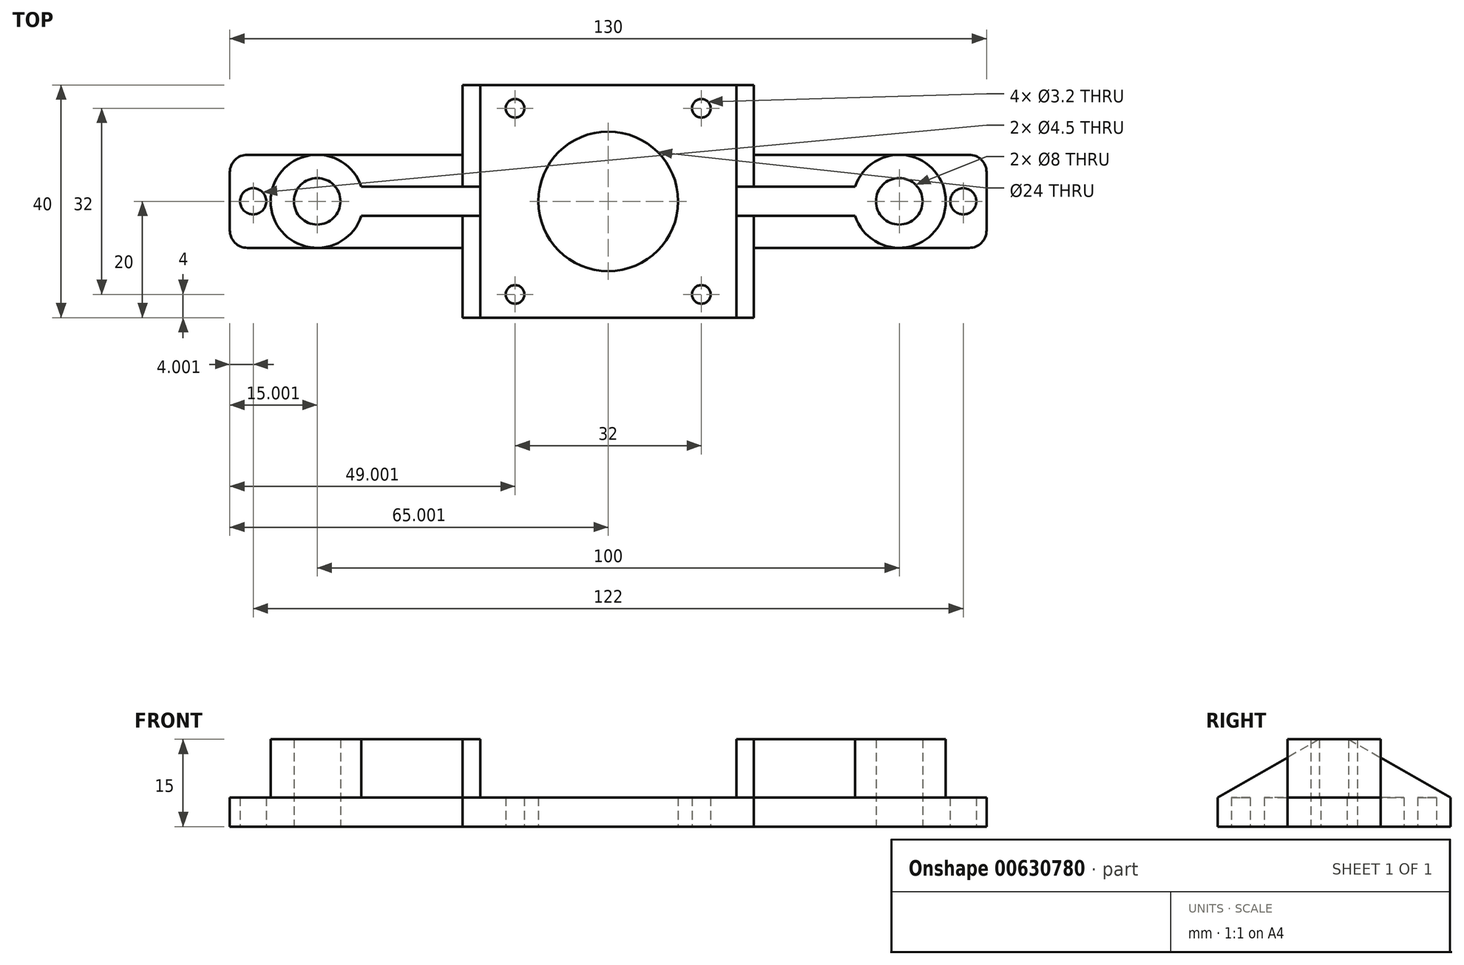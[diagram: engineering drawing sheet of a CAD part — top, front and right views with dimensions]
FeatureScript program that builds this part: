
annotation { "Feature Type Name" : "Feature", "Feature Type Description" : "" }
export const myFeature = defineFeature(function(context is Context, id is Id, definition is map)
    precondition{}
    {
        {
            var Q0;
            Q0=qCreatedBy(makeId("Top.planeOp"),FACE);
            var sketch = newSketch(context, id + "F0", { "sketchPlane" : qUnion([Q0])});
            skCircle(sketch, "E0", {"center": v(-20.16, 0) * mm, "radius": 4 * mm});
            skCircle(sketch, "E1", {"center": v(-20.16, 0) * mm, "radius": 8 * mm});
            skCircle(sketch, "E2", {"center": v(79.84, 0) * mm, "radius": 4 * mm});
            skCircle(sketch, "E3", {"center": v(79.84, 0) * mm, "radius": 8 * mm});
            skLineSegment(sketch, "E4.bottom", {"start": v(-32.16, 8) * mm, "end": v(4.84, 8) * mm});
            skLineSegment(sketch, "E4.top", {"start": v(-32.16, -8) * mm, "end": v(4.84, -8) * mm});
            skLineSegment(sketch, "E4.left", {"start": v(-35.16, 5) * mm, "end": v(-35.16, -5) * mm});
            skLineSegment(sketch, "E4.right", {"start": v(94.84, 5) * mm, "end": v(94.84, -5) * mm});
            skCircle(sketch, "E5", {"center": v(-31.16, 0) * mm, "radius": 2.25 * mm});
            skCircle(sketch, "E6", {"center": v(90.84, 0) * mm, "radius": 2.25 * mm});
            skPoint(sketch, "E7.visualSharp", {"position": v(94.84, 8) * mm});
            skArc(sketch, "E7.filletArc", {"start": v(94.84, 5) * mm, "mid": v(93.96, 7.12) * mm, "end": v(91.84, 8) * mm});
            skPoint(sketch, "E8.visualSharp", {"position": v(94.84, -8) * mm});
            skArc(sketch, "E8.filletArc", {"start": v(91.84, -8) * mm, "mid": v(93.96, -7.12) * mm, "end": v(94.84, -5) * mm});
            skPoint(sketch, "E9.visualSharp", {"position": v(-35.16, -8) * mm});
            skArc(sketch, "E9.filletArc", {"start": v(-35.16, -5) * mm, "mid": v(-34.28, -7.12) * mm, "end": v(-32.16, -8) * mm});
            skPoint(sketch, "E10.visualSharp", {"position": v(-35.16, 8) * mm});
            skArc(sketch, "E10.filletArc", {"start": v(-32.16, 8) * mm, "mid": v(-34.28, 7.12) * mm, "end": v(-35.16, 5) * mm});
            skPoint(sketch, "E11.center.orphan", {"position": v(-10.69, 0) * mm});
            skPoint(sketch, "E12.center.orphan", {"position": v(67.31, 0) * mm});
            skLineSegment(sketch, "E13.bottom", {"start": v(-12.56, 2.5) * mm, "end": v(4.84, 2.5) * mm});
            skLineSegment(sketch, "E13.top", {"start": v(-12.56, -2.5) * mm, "end": v(4.84, -2.5) * mm});
            skLineSegment(sketch, "E13.left", {"start": v(-12.56, 2.58) * mm, "end": v(-12.56, 2.5) * mm});
            skLineSegment(sketch, "E14.top", {"start": v(4.84, -20) * mm, "end": v(54.84, -20) * mm});
            skLineSegment(sketch, "E14.left", {"start": v(4.84, 8) * mm, "end": v(4.84, 2.5) * mm});
            skLineSegment(sketch, "E14.right", {"start": v(54.84, 8) * mm, "end": v(54.84, 2.5) * mm});
            skLineSegment(sketch, "E15.trimOffspring", {"start": v(54.84, -8) * mm, "end": v(91.84, -8) * mm});
            skLineSegment(sketch, "E16.top", {"start": v(4.84, 20) * mm, "end": v(54.84, 20) * mm});
            skLineSegment(sketch, "E16.left", {"start": v(4.84, 8) * mm, "end": v(4.84, 20) * mm});
            skLineSegment(sketch, "E16.right", {"start": v(54.84, 8) * mm, "end": v(54.84, 20) * mm});
            skLineSegment(sketch, "E17.trimOffspring", {"start": v(54.84, 8) * mm, "end": v(91.84, 8) * mm});
            skCircle(sketch, "E18", {"center": v(29.84, 0) * mm, "radius": 12 * mm});
            skLineSegment(sketch, "E19.trimOffspring", {"start": v(54.84, 2.5) * mm, "end": v(72.24, 2.5) * mm});
            skLineSegment(sketch, "E20.trimOffspring", {"start": v(54.84, -2.5) * mm, "end": v(72.24, -2.5) * mm});
            skLineSegment(sketch, "E21", {"start": v(7.84, 20) * mm, "end": v(7.84, -20) * mm});
            skLineSegment(sketch, "E22.trimOffspring", {"start": v(4.84, -2.5) * mm, "end": v(4.84, -20) * mm});
            skLineSegment(sketch, "E23", {"start": v(51.84, 20) * mm, "end": v(51.84, -20) * mm});
            skLineSegment(sketch, "E24.trimOffspring", {"start": v(54.84, -2.5) * mm, "end": v(54.84, -20) * mm});
            skCircle(sketch, "E25", {"center": v(13.84, 16) * mm, "radius": 1.6 * mm});
            skCircle(sketch, "E26.1.0", {"center": v(13.84, -16) * mm, "radius": 1.6 * mm});
            skCircle(sketch, "E26.2.0", {"center": v(45.84, -16) * mm, "radius": 1.6 * mm});
            skCircle(sketch, "E26.3.0", {"center": v(45.84, 16) * mm, "radius": 1.6 * mm});
            skPoint(sketch, "E27.orphan", {"position": v(-14.09, -2.5) * mm});
            skSolve(sketch);
        }
        {
            var Q0;
            {var subQ0=sQuery(id+"F0.wireOp",EDGE,"E13.top");Q0=makeQuery(id+"F0.imprint","IMPRINT",FACE,{"disambiguationData":[TD([[makeQuery(id+"F0.imprint","IMPRINT",EDGE,{"derivedFrom":subQ0}),-1.0]])]});}
            var Q1;
            {var subQ0=sQuery(id+"F0.wireOp",EDGE,"E13.bottom");Q1=makeQuery(id+"F0.imprint","IMPRINT",FACE,{"disambiguationData":[TD([[makeQuery(id+"F0.imprint","IMPRINT",EDGE,{"derivedFrom":subQ0}),1.0]])]});}
            var Q2;
            Q2=makeQuery(id+"F0.imprint","IMPRINT",FACE,{"disambiguationData":[TD([[makeQuery(id+"F0.imprint","IMPRINT",EDGE,{"derivedFrom":sQuery(id+"F0.wireOp",EDGE,"E4.left")}),1.0]])]});
            var Q3;
            Q3=makeQuery(id+"F0.imprint","IMPRINT",FACE,{"disambiguationData":[TD([[makeQuery(id+"F0.imprint","IMPRINT",EDGE,{"derivedFrom":sQuery(id+"F0.wireOp",EDGE,"E4.right")}),-1.0]])]});
            var Q4;
            {var subQ0=sQuery(id+"F0.wireOp",EDGE,"E20.trimOffspring");Q4=makeQuery(id+"F0.imprint","IMPRINT",FACE,{"disambiguationData":[TD([[makeQuery(id+"F0.imprint","IMPRINT",EDGE,{"derivedFrom":subQ0}),-1.0]])]});}
            var Q5;
            {var subQ4=sQuery(id+"F0.wireOp",EDGE,"E14.right");Q5=makeQuery(id+"F0.imprint","IMPRINT",FACE,{"disambiguationData":[TD([[makeQuery(id+"F0.imprint","IMPRINT",EDGE,{"derivedFrom":subQ4}),1.0]])]});}
            var Q6;
            Q6=makeQuery(id+"F0.imprint","IMPRINT",FACE,{"disambiguationData":[TD([[makeQuery(id+"F0.imprint","IMPRINT",EDGE,{"derivedFrom":sQuery(id+"F0.wireOp",EDGE,"E18")}),-1.0]])]});
            extrude(context, id + "F1", {"entities" : qUnion([Q0, Q1, Q2, Q3, Q4, Q5, Q6]), "depth" : 5 * mm, "offsetDistance" : 25 * mm});
        }
        {
            var Q0;
            Q0=makeQuery(id+"F0.imprint","IMPRINT",FACE,{"disambiguationData":[TD([[makeQuery(id+"F0.imprint","IMPRINT",EDGE,{"derivedFrom":sQuery(id+"F0.wireOp",EDGE,"E0")}),-1.0]])]});
            var Q1;
            Q1=makeQuery(id+"F0.imprint","IMPRINT",FACE,{"disambiguationData":[TD([[makeQuery(id+"F0.imprint","IMPRINT",EDGE,{"derivedFrom":sQuery(id+"F0.wireOp",EDGE,"E2")}),-1.0]])]});
            var Q2;
            {var subQ1=sQuery(id+"F0.wireOp",EDGE,"E13.bottom");Q2=makeQuery(id+"F0.imprint","IMPRINT",FACE,{"disambiguationData":[TD([[makeQuery(id+"F0.imprint","IMPRINT",EDGE,{"derivedFrom":subQ1}),-1.0]])]});}
            var Q3;
            {var subQ0=sQuery(id+"F0.wireOp",EDGE,"E19.trimOffspring");Q3=makeQuery(id+"F0.imprint","IMPRINT",FACE,{"disambiguationData":[TD([[makeQuery(id+"F0.imprint","IMPRINT",EDGE,{"derivedFrom":subQ0}),-1.0]])]});}
            extrude(context, id + "F2", {"entities" : qUnion([Q0, Q1, Q2, Q3]), "operationType" : NewBodyOperationType.ADD, "depth" : 15 * mm, "offsetDistance" : 25 * mm});
        }
        {
            var Q0;
            {var subQ0=sQuery(id+"F0.wireOp",EDGE,"E14.top");Q0=makeQuery(id+"F2.opExtrude","CAP_EDGE",EDGE,{"disambiguationData":[OSD([subQ0]),TDD([makeQuery(id+"F0.imprint","IMPRINT",EDGE,{"disambiguationData":[TD([[makeQuery(id+"F0.imprint","INTERSECT",VERTEX,{"derivedFrom":[subQ0,sQuery(id+"F0.wireOp",EDGE,"E22.trimOffspring")]}),-1.0]])],"derivedFrom":subQ0})])],"isStart":false});}
            var Q1;
            {var subQ0=sQuery(id+"F0.wireOp",EDGE,"E16.top");Q1=makeQuery(id+"F2.opExtrude","CAP_EDGE",EDGE,{"disambiguationData":[OSD([subQ0]),TDD([makeQuery(id+"F0.imprint","IMPRINT",EDGE,{"disambiguationData":[TD([[makeQuery(id+"F0.imprint","INTERSECT",VERTEX,{"derivedFrom":[subQ0,sQuery(id+"F0.wireOp",EDGE,"E16.left")]}),-1.0]])],"derivedFrom":subQ0})])],"isStart":false});}
            chamfer(context, id + "F3", {"entities" : qUnion([Q0, Q1]), "chamferType" : ChamferType.TWO_OFFSETS, "width1" : 17.5 * mm, "oppositeDirection" : false, "width2" : 10 * mm, "tangentPropagation" : true});
        }
        {
            var Q0;
            {var subQ0=sQuery(id+"F0.wireOp",EDGE,"E14.top");Q0=makeQuery(id+"F2.opExtrude","CAP_EDGE",EDGE,{"disambiguationData":[OSD([subQ0]),TDD([makeQuery(id+"F0.imprint","IMPRINT",EDGE,{"disambiguationData":[TD([[makeQuery(id+"F0.imprint","INTERSECT",VERTEX,{"derivedFrom":[subQ0,sQuery(id+"F0.wireOp",EDGE,"E24.trimOffspring")]}),1.0]])],"derivedFrom":subQ0})])],"isStart":false});}
            var Q1;
            {var subQ0=sQuery(id+"F0.wireOp",EDGE,"E16.top");Q1=makeQuery(id+"F2.opExtrude","CAP_EDGE",EDGE,{"disambiguationData":[OSD([subQ0]),TDD([makeQuery(id+"F0.imprint","IMPRINT",EDGE,{"disambiguationData":[TD([[makeQuery(id+"F0.imprint","INTERSECT",VERTEX,{"derivedFrom":[subQ0,sQuery(id+"F0.wireOp",EDGE,"E16.right")]}),1.0]])],"derivedFrom":subQ0})])],"isStart":false});}
            chamfer(context, id + "F4", {"entities" : qUnion([Q0, Q1]), "chamferType" : ChamferType.TWO_OFFSETS, "width1" : 17.5 * mm, "oppositeDirection" : false, "width2" : 10 * mm, "tangentPropagation" : true});
        }
    });
